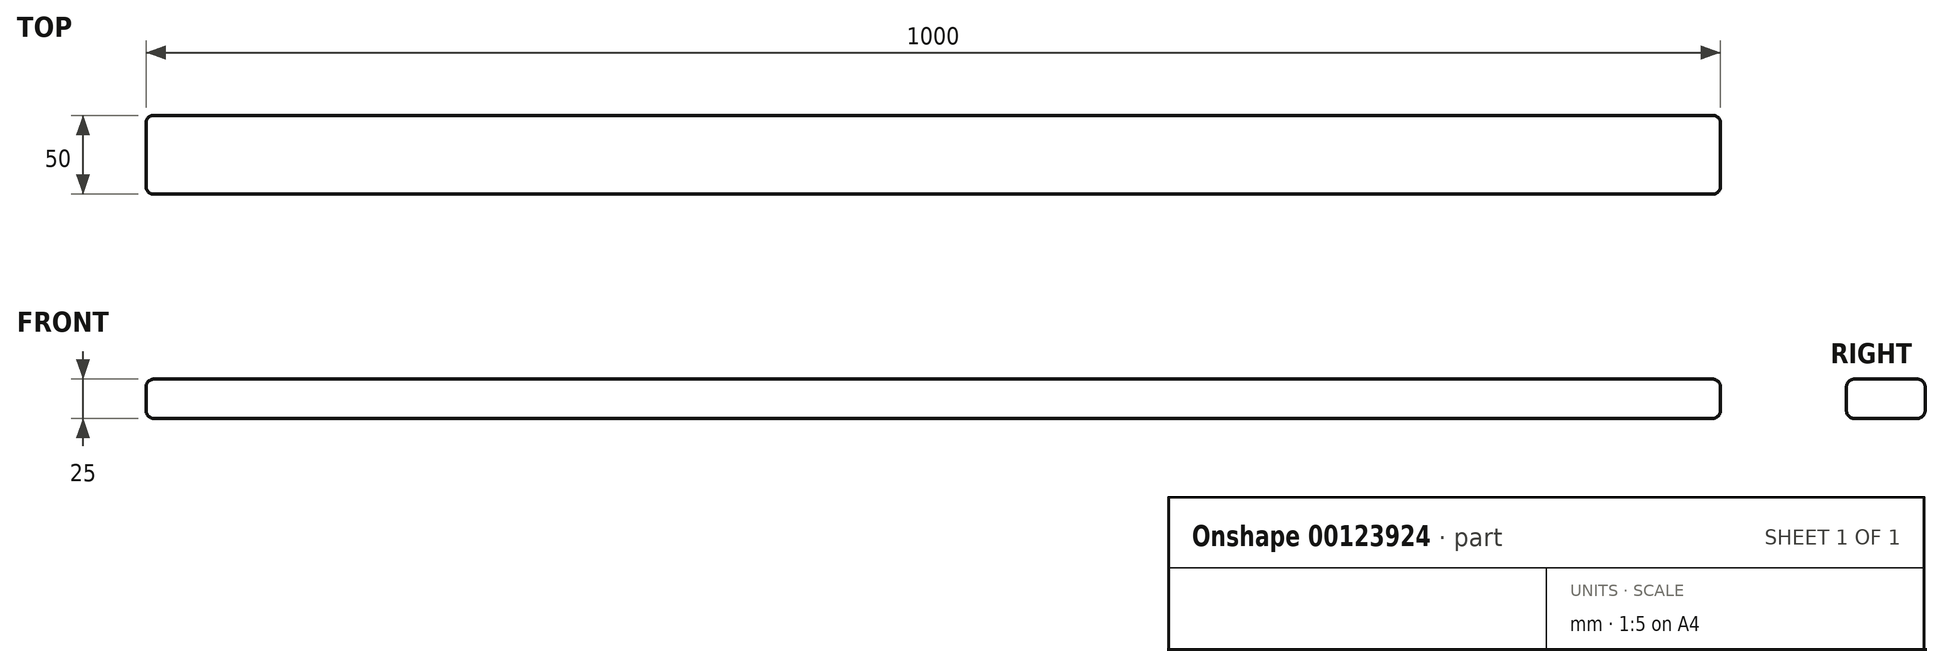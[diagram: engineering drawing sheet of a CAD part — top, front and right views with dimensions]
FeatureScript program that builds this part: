
annotation { "Feature Type Name" : "Feature", "Feature Type Description" : "" }
export const myFeature = defineFeature(function(context is Context, id is Id, definition is map)
    precondition{}
    {
        {
            var Q0;
            Q0=qCreatedBy(makeId("Right.planeOp"),FACE);
            var sketch = newSketch(context, id + "F0", { "sketchPlane" : qUnion([Q0])});
            skLineSegment(sketch, "E0.bottom", {"start": v(20, -12.5) * mm, "end": v(-20, -12.5) * mm});
            skLineSegment(sketch, "E0.top", {"start": v(20, 12.5) * mm, "end": v(-20, 12.5) * mm});
            skLineSegment(sketch, "E0.left", {"start": v(25, -7.5) * mm, "end": v(25, 7.5) * mm});
            skLineSegment(sketch, "E0.right", {"start": v(-25, -7.5) * mm, "end": v(-25, 7.5) * mm});
            skPoint(sketch, "E0.middle", {"position": v(0, 0) * mm});
            skPoint(sketch, "E1.visualSharp", {"position": v(-25, 12.5) * mm});
            skArc(sketch, "E1.filletArc", {"start": v(-20, 12.5) * mm, "mid": v(-23.54, 11.04) * mm, "end": v(-25, 7.5) * mm});
            skPoint(sketch, "E2.visualSharp", {"position": v(25, 12.5) * mm});
            skArc(sketch, "E2.filletArc", {"start": v(25, 7.5) * mm, "mid": v(23.54, 11.04) * mm, "end": v(20, 12.5) * mm});
            skPoint(sketch, "E3.visualSharp", {"position": v(-25, -12.5) * mm});
            skArc(sketch, "E3.filletArc", {"start": v(-25, -7.5) * mm, "mid": v(-23.54, -11.04) * mm, "end": v(-20, -12.5) * mm});
            skPoint(sketch, "E4.visualSharp", {"position": v(25, -12.5) * mm});
            skArc(sketch, "E4.filletArc", {"start": v(20, -12.5) * mm, "mid": v(23.54, -11.04) * mm, "end": v(25, -7.5) * mm});
            skSolve(sketch);
        }
        {
            var Q0;
            Q0=makeQuery(id+"F0.imprint","IMPRINT",FACE,{"disambiguationData":[TD([[makeQuery(id+"F0.imprint","IMPRINT",EDGE,{"derivedFrom":sQuery(id+"F0.wireOp",EDGE,"E0.bottom")}),-1.0]])]});
            extrude(context, id + "F1", {"entities" : qUnion([Q0]), "depth" : 1000 * mm});
        }
        {
            var Q0;
            Q0=makeQuery(id+"F1.opExtrude","CAP_EDGE",EDGE,{"disambiguationData":[OSD([sQuery(id+"F0.wireOp",EDGE,"E0.right")])],"isStart":false});
            var Q1;
            Q1=makeQuery(id+"F1.opExtrude","CAP_EDGE",EDGE,{"disambiguationData":[OSD([sQuery(id+"F0.wireOp",EDGE,"E0.left")])],"isStart":true});
            fillet(context, id + "F2", {"entities" : qUnion([Q0, Q1]), "radius" : 5 * mm, "tangentPropagation" : true, "allowEdgeOverflow" : false});
        }
    });
